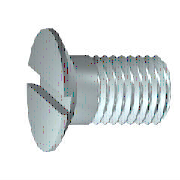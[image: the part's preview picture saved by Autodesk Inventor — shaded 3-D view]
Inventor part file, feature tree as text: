
AUTODESK INVENTOR PART (.ipt)
format: ipt  version: 2017 (Build 210142000, 142)  size: 177,664 bytes
history: native  units: mm (DEFAULTED — no unit token found)
features: sketch x2, extrude x1, plane x1
ambient origin geometry x7: Origin, YZ Plane, XZ Plane, X Axis, Y Axis, Z Axis, Center Point
bodies: Solid1 (feature_tree), Body (feature_tree)
feature tree (4):
  extrude  "Slot"  Depth=6.0mm
  plane  "Work Plane1"
  sketch  "Sketch1"  dims[d0=6.0mm d1=45.0deg d2=0.36807mm d3=2.87mm d4=1.93mm d5=2.76386mm]
  sketch  "Sketch2"  dims[d6=3.5mm d7=6.1mm d19=90.0deg d8=0.7mm d9=0.0mm d10=2.87mm d11=0.0mm d12=0.36807mm d13=0.184035mm d15=1.0mm d16=6.1mm d17=0.0mm d35=45.0deg d39=0.0mm d40=0.0mm]
